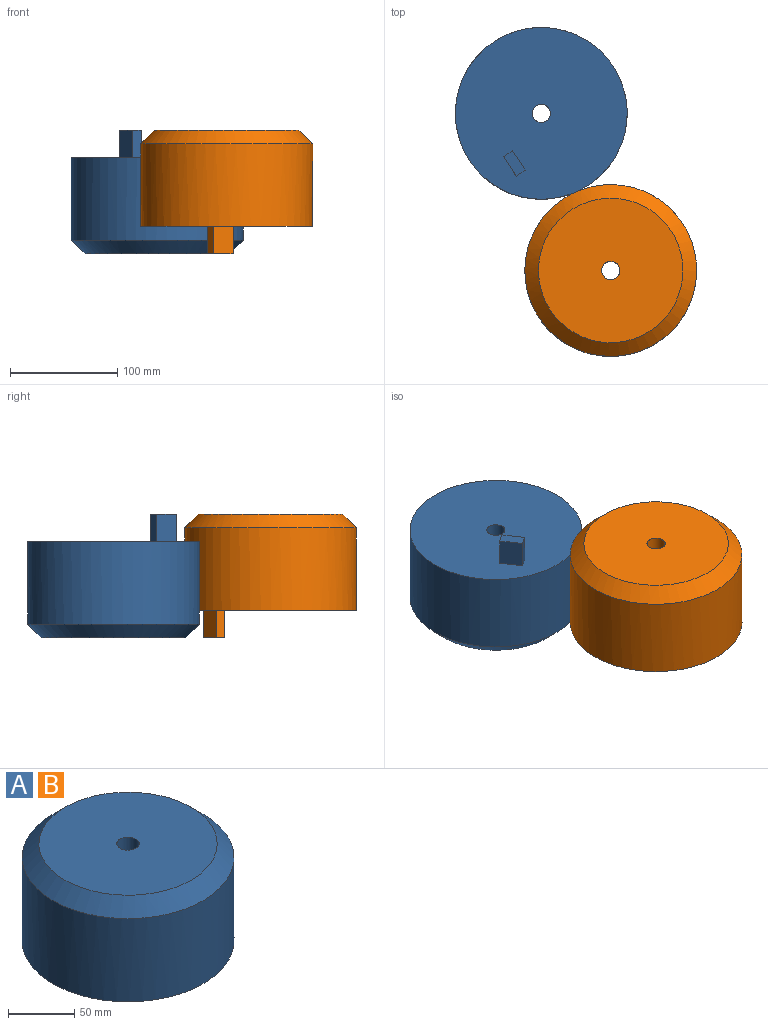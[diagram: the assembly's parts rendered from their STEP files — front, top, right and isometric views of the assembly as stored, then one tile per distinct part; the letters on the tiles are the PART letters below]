
ASSEMBLY  parts=2 mates=1
PART A: 10 faces, bbox 159.8x159.8x114.8 mm
  f0: plane 159.84x159.84mm, normal (0,0,-1), area 19625mm2, adj f2,f4,f5,f6,f7,f8
  f1: plane 134.44x134.44mm, normal (0,0,1), area 13969.9mm2, adj f3,f4
  f2: cylinder r=79.92mm len=159.84mm, axis (0,0,1), area 38527.4mm2, adj f0,f3
  f3: cone r=67.22mm half-angle=45deg, axis (0,0,-1), area 8302.5mm2, adj f1,f2
  f4: cylinder r=8.48mm len=89.42mm, axis (0,0,1), area 4765.8mm2, adj f0,f1
  f5: plane 25.4x21.61mm, normal (1,0,0), area 548.9mm2, adj f0,f6,f8,f9
  f6: plane 25.4x9.98mm, normal (0,-1,0), area 253.4mm2, adj f0,f5,f7,f9
  f7: plane 25.4x21.61mm, normal (-1,0,0), area 548.9mm2, adj f0,f6,f8,f9
  f8: plane 25.4x9.98mm, normal (0,1,0), area 253.4mm2, adj f0,f5,f7,f9
  f9: plane 21.61x9.98mm, normal (0,0,-1), area 215.6mm2, adj f5,f6,f7,f8
PART B: same geometry as A
PLACE A rot(axis=(0.29,-0.96,0),180deg) t=(-29.12,170.17,-61.68)mm
PLACE B rot(axis=(0,0,1),124deg) t=(23.96,-35.48,-27.74)mm
MATE planar A.f2 <-> B.f9  axis (0,0,1) through (-64.6,146.21,-102.12)mm
